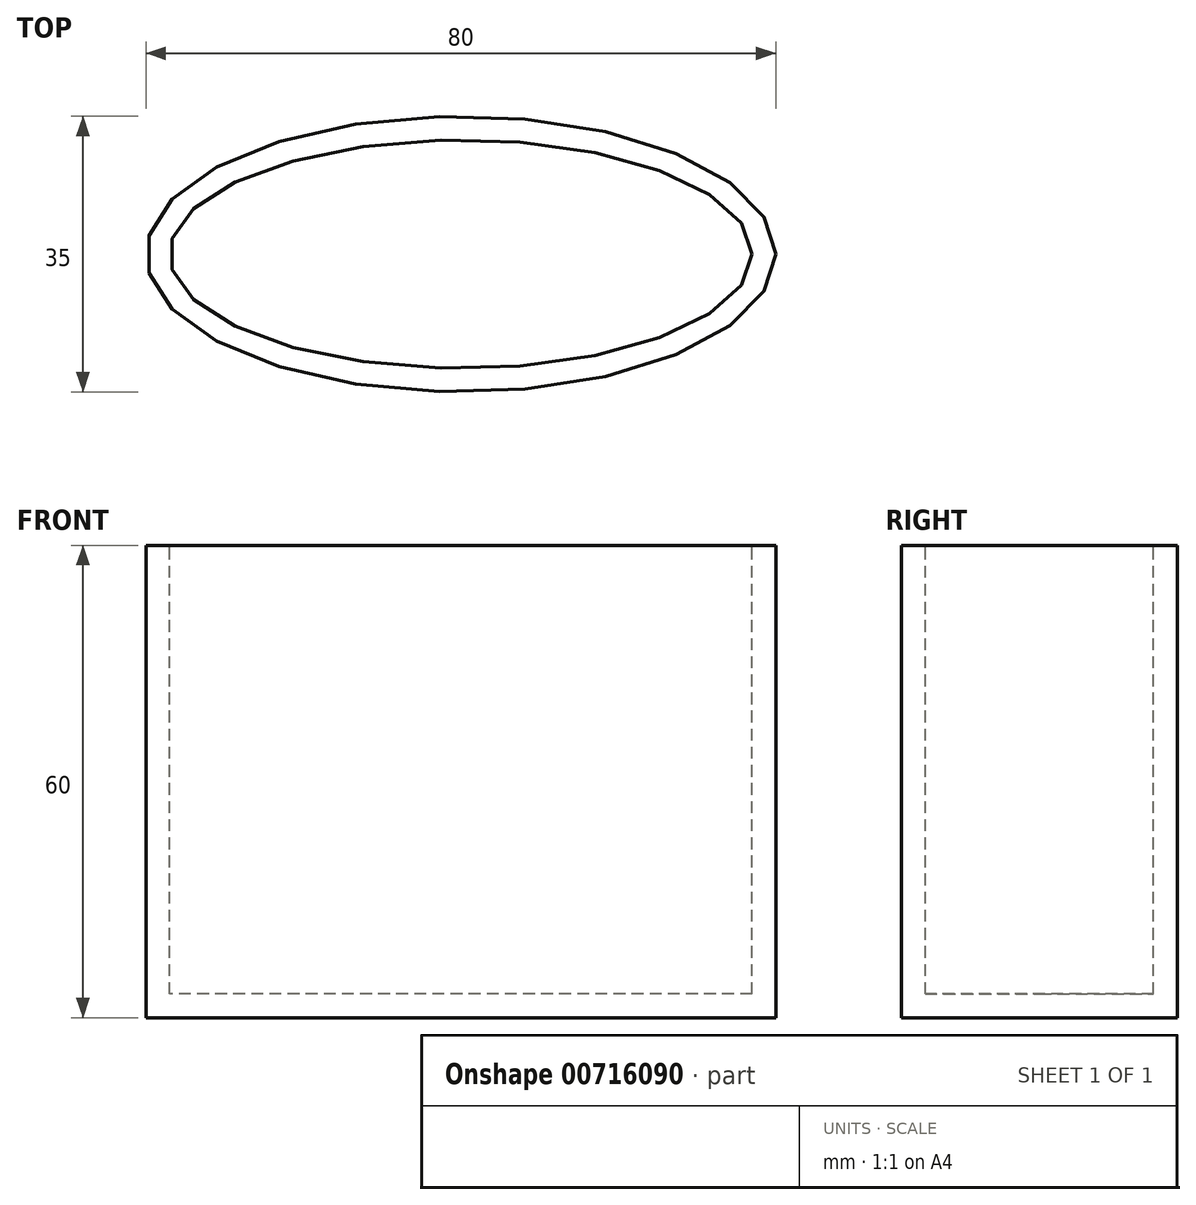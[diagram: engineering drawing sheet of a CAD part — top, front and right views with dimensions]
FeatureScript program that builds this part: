
annotation { "Feature Type Name" : "Feature", "Feature Type Description" : "" }
export const myFeature = defineFeature(function(context is Context, id is Id, definition is map)
    precondition{}
    {
        {
            var Q0;
            Q0=qCreatedBy(makeId("Top.planeOp"),FACE);
            var sketch = newSketch(context, id + "F0", { "sketchPlane" : qUnion([Q0])});
            skEllipse(sketch, "E0", {"center": v(0, 0) * mm, "majorRadius": 40 * mm, "minorRadius": 17.5 * mm, "majorAxis": v(1, 0)});
            skPoint(sketch, "E1", {"position": v(-40, 0) * mm});
            skPoint(sketch, "E2", {"position": v(40, 0) * mm});
            skPoint(sketch, "E3", {"position": v(0, 17.5) * mm});
            skPoint(sketch, "E4", {"position": v(0, -17.5) * mm});
            skSolve(sketch);
        }
        {
            var Q0;
            Q0 = qSketchRegion(id + "F0", true);
            extrude(context, id + "F1", {"entities" : qUnion([Q0]), "depth" : 80 * mm, "offsetDistance" : 25 * mm});
        }
        {
            var Q0;
            Q0=makeQuery(id+"F1.opExtrude","CAP_FACE",FACE,{"disambiguationData":[OSD([sQuery(id+"F0.wireOp",EDGE,"E0")])],"isStart":false});
            var sketch = newSketch(context, id + "F2", { "sketchPlane" : qUnion([Q0])});
            skEllipse(sketch, "E5", {"center": v(0, 0) * mm, "majorRadius": 37 * mm, "minorRadius": 14.5 * mm, "majorAxis": v(1, 0)});
            skPoint(sketch, "E6", {"position": v(-40, 0) * mm});
            skPoint(sketch, "E7", {"position": v(-37, 0) * mm});
            skPoint(sketch, "E8", {"position": v(37, 0) * mm});
            skPoint(sketch, "E9", {"position": v(40, 0) * mm});
            skPoint(sketch, "E10", {"position": v(0, 14.5) * mm});
            skPoint(sketch, "E11", {"position": v(0, 17.5) * mm});
            skPoint(sketch, "E12", {"position": v(0, -17.5) * mm});
            skPoint(sketch, "E13", {"position": v(0, -14.5) * mm});
            skSolve(sketch);
        }
        {
            var Q0;
            Q0 = qSketchRegion(id + "F2", true);
            extrude(context, id + "F3", {"entities" : qUnion([Q0]), "operationType" : NewBodyOperationType.REMOVE, "oppositeDirection" : true, "depth" : 77 * mm, "offsetDistance" : 25 * mm});
        }
        {
            var Q0;
            Q0=makeQuery(id+"F1.opExtrude","CAP_FACE",FACE,{"disambiguationData":[OSD([sQuery(id+"F0.wireOp",EDGE,"E0")])],"isStart":false});
            var sketch = newSketch(context, id + "F4", { "sketchPlane" : qUnion([Q0])});
            skLineSegment(sketch, "E14.bottom", {"start": v(-48.88, 94.28) * mm, "end": v(87.51, 94.28) * mm});
            skLineSegment(sketch, "E14.top", {"start": v(-48.88, -111.36) * mm, "end": v(87.51, -111.36) * mm});
            skLineSegment(sketch, "E14.left", {"start": v(-48.88, 94.28) * mm, "end": v(-48.88, -111.36) * mm});
            skLineSegment(sketch, "E14.right", {"start": v(87.51, 94.28) * mm, "end": v(87.51, -111.36) * mm});
            skSolve(sketch);
        }
        {
            var Q0;
            Q0 = qSketchRegion(id + "F4", true);
            extrude(context, id + "F5", {"entities" : qUnion([Q0]), "operationType" : NewBodyOperationType.REMOVE, "oppositeDirection" : true, "depth" : 20 * mm, "offsetDistance" : 25 * mm});
        }
    });
